# Revit family: Drain_Floor_Top_Diameter_9_Inch-Zurn-Z551-Medium-Duty
name_source: partatom
category: Plumbing Fixtures
units: mm (PartAtom-declared; Revit-internal decimal feet)

## family parameters
Always vertical = Yes
Cut with Voids When Loaded = No
Maintain Annotation Orientation = No
OmniClass Number = 23.45.55.21
OmniClass Title = Drains (Wastes)
Part Type = Normal
Room Calculation Point = No
Round Connector Dimension = Use Radius
Shared = No
Work Plane-Based = No

## types (33) — shared parameters
Assembly Code = D2030300
CW Connection = No
Default Elevation = 25 "
Description = 9 [229] DIAMETER TOP MEDIUM-DUTY DRAIN
Grate Open Area Sq.in = 18 "
HW Connection = No
Main Material = Iron - Zurn -Cast - Painted - Blue
Manufacturer = Zurn Water, LLC
Manufacurer Brand = Zurn
Modified Date = 11/21/2025
P Trap Primer Connetor = 0.25 "
Product Documentation Link = https://files.zurn.com
Product Page URL = https://www.zurn.com
Product data url = https://www.bimobject.com
URL = www.zurn.com
Vent Connection = No
WFU = 1
Waste Connection = Yes
Width = 12 "
zero-valued in all types: CWFU, HWFU

## per-type parameters (varying)
| type | Approx. Weight (Lbs) | Body Height (E) | Frame Dimension | Frame and Grate | Model | Outlet Connector Radius | Pipe Size A (Actual) | Pipe Size A (Inner Diameter) | Pipe Size A (Nominal Diameter) | Top Diameter | Top Diameter Inner | Type Comments | Z-Grate | ZN-Grate |
| Z551-2NH | 28 " | 4.75 " | 2 " | Iron - Zurn -Cast - Painted - Blue | Z551 | 1 " | 2.375 " | 2.067 " | 2 " | 9 " | 8.625 " | Z551-2 Inch-No Hub Outlet | Yes | No |
| Z551-2NL | 28 " | 3.5 " | 2 " | Iron - Zurn -Cast - Painted - Blue | Z551 | 1 " | 2.375 " | 2.067 " | 2 " | 9 " | 8.625 " | Z551-2 Inch -Neo Loc Outlet | Yes | No |
| Z551-3NH | 28 " | 4.75 " | 2 " | Iron - Zurn -Cast - Painted - Blue | Z551 | 1.5 " | 3.5 " | 3.068 " | 3 " | 9 " | 8.625 " | Z551-3 Inch -No-Hub Outlet | Yes | No |
| Z551-3NL | 28 " | 3.5 " | 2 " | Iron - Zurn -Cast - Painted - Blue | Z551 | 1.5 " | 3.5 " | 3.068 " | 3 " | 9 " | 8.625 " | Z551-3 Inch -Neo-Loc Outlet | Yes | No |
| Z551-3IC | 28 " | 3.75 " | 2 " | Iron - Zurn -Cast - Painted - Blue | Z551 | 1.5 " | 3.5 " | 3.068 " | 3 " | 9 " | 8.625 " | Z551-3 Inch -Inside Caulk Outlet | Yes | No |
| Z551-3IP | 28 " | 2.75 " | 2 " | Iron - Zurn -Cast - Painted - Blue | Z551 | 1.5 " | 3.5 " | 3.068 " | 3 " | 9 " | 8.625 " | Z551-3 Inch -Threaded Outlet | Yes | No |
| Z551-4IC | 28 " | 3.75 " | 2 " | Iron - Zurn -Cast - Painted - Blue | Z551 | 2 " | 4.5 " | 4.026 " | 4 " | 9 " | 8.625 " | Z551-4 Inch -Inside Caulk Outlet | Yes | No |
| Z551-4NH | 28 " | 4.75 " | 2 " | Iron - Zurn -Cast - Painted - Blue | Z551 | 2 " | 4.5 " | 4.026 " | 4 " | 9 " | 8.625 " | Z551-4 Inch -No-Hub Outlet | Yes | No |
| Z551-4IP | 28 " | 2.75 " | 2 " | Iron - Zurn -Cast - Painted - Blue | Z551 | 2 " | 4.5 " | 4.026 " | 4 " | 9 " | 8.625 " | Z551-4 Inch -Threaded Outlet | Yes | No |
| Z551-4NL | 28 " | 3.5 " | 2 " | Iron - Zurn -Cast - Painted - Blue | Z551 | 2 " | 4.5 " | 4.026 " | 4 " | 9 " | 8.625 " | Z551-4 Inch -Neo-Loc Outlet | Yes | No |
| Z551-6NH | 30 " | 5.25 " | 2 " | Iron - Zurn -Cast - Painted - Blue | Z551 | 3 " | 6.625 " | 6.065 " | 6 " | 9 " | 8.625 " | Z551-6 Inch -No Hub Outlet | Yes | No |
| ZB551-2NH | 28 " | 4.75 " | 2.188 " | Bronze - Zurn - Polished | ZB551 | 1 " | 2.375 " | 2.067 " | 2 " | 9.75 " | 9.375 " | ZB551-2 Inch-No Hub Outlet | No | Yes |
| ZB551-2NL | 28 " | 3.5 " | 2.188 " | Bronze - Zurn - Polished | ZB551 | 1 " | 2.375 " | 2.067 " | 2 " | 9.75 " | 9.375 " | ZB551-2 Inch -Neo Loc Outlet | No | Yes |
| ZB551-3NH | 28 " | 4.75 " | 2.188 " | Bronze - Zurn - Polished | ZB551 | 1.5 " | 3.5 " | 3.068 " | 3 " | 9.75 " | 9.375 " | ZB551-3 Inch -No-Hub Outlet | No | Yes |
| ZB551-3NL | 28 " | 3.5 " | 2.188 " | Bronze - Zurn - Polished | ZB551 | 1.5 " | 3.5 " | 3.068 " | 3 " | 9.75 " | 9.375 " | ZB551-3 Inch -Neo-Loc Outlet | No | Yes |
| ZB551-3IC | 28 " | 3.75 " | 2.188 " | Bronze - Zurn - Polished | ZB551 | 1.5 " | 3.5 " | 3.068 " | 3 " | 9.75 " | 9.375 " | ZB551-3 Inch -Inside Caulk Outlet | No | Yes |
| ZB551-3IP | 28 " | 2.75 " | 2.188 " | Bronze - Zurn - Polished | ZB551 | 1.5 " | 3.5 " | 3.068 " | 3 " | 9.75 " | 9.375 " | ZB551-3 Inch -Threaded Outlet | No | Yes |
| ZB551-4IC | 28 " | 3.75 " | 2.188 " | Bronze - Zurn - Polished | ZB551 | 2 " | 4.5 " | 4.026 " | 4 " | 9.75 " | 9.375 " | ZB551-4 Inch -Inside Caulk Outlet | No | Yes |
| ZB551-4NH | 28 " | 4.75 " | 2.188 " | Bronze - Zurn - Polished | ZB551 | 2 " | 4.5 " | 4.026 " | 4 " | 9.75 " | 9.375 " | ZB551-4 Inch -No-Hub Outlet | No | Yes |
| ZB551-4IP | 28 " | 2.75 " | 2.188 " | Bronze - Zurn - Polished | ZB551 | 2 " | 4.5 " | 4.026 " | 4 " | 9.75 " | 9.375 " | ZB551-4 Inch -Threaded Outlet | No | Yes |
| ZB551-4NL | 28 " | 3.5 " | 2.188 " | Bronze - Zurn - Polished | ZB551 | 2 " | 4.5 " | 4.026 " | 4 " | 9.75 " | 9.375 " | ZB551-4 Inch -Neo-Loc Outlet | No | Yes |
| ZB551-6NH | 30 " | 5.25 " | 2.188 " | Bronze - Zurn - Polished | ZB551 | 3 " | 6.625 " | 6.065 " | 6 " | 9.75 " | 9.375 " | ZB551-6 Inch -No Hub Outlet | No | Yes |
| ZN551-2NH | 28 " | 4.75 " | 2.188 " | Bronze - Zurn - Polished Nickel | ZN551 | 1 " | 2.375 " | 2.067 " | 2 " | 9.75 " | 9.375 " | ZN551-2 Inch-No Hub Outlet | No | Yes |
| ZN551-2NL | 28 " | 3.5 " | 2.188 " | Bronze - Zurn - Polished Nickel | ZN551 | 1 " | 2.375 " | 2.067 " | 2 " | 9.75 " | 9.375 " | ZN551-2 Inch -Neo Loc Outlet | No | Yes |
| ZN551-3NH | 28 " | 4.75 " | 2.188 " | Bronze - Zurn - Polished Nickel | ZN551 | 1.5 " | 3.5 " | 3.068 " | 3 " | 9.75 " | 9.375 " | ZN551-3 Inch -No-Hub Outlet | No | Yes |
| ZN551-3NL | 28 " | 3.5 " | 2.188 " | Bronze - Zurn - Polished Nickel | ZN551 | 1.5 " | 3.5 " | 3.068 " | 3 " | 9.75 " | 9.375 " | ZN551-3 Inch -Neo-Loc Outlet | No | Yes |
| ZN551-3IC | 28 " | 3.75 " | 2.188 " | Bronze - Zurn - Polished Nickel | ZN551 | 1.5 " | 3.5 " | 3.068 " | 3 " | 9.75 " | 9.375 " | ZN551-3 Inch -Inside Caulk Outlet | No | Yes |
| ZN551-3IP | 28 " | 2.75 " | 2.188 " | Bronze - Zurn - Polished Nickel | ZN551 | 1.5 " | 3.5 " | 3.068 " | 3 " | 9.75 " | 9.375 " | ZN551-3 Inch -Threaded Outlet | No | Yes |
| ZN551-4IC | 28 " | 3.75 " | 2.188 " | Bronze - Zurn - Polished Nickel | ZN551 | 2 " | 4.5 " | 4.026 " | 4 " | 9.75 " | 9.375 " | ZN551-4 Inch -Inside Caulk Outlet | No | Yes |
| ZN551-4NH | 28 " | 4.75 " | 2.188 " | Bronze - Zurn - Polished Nickel | ZN551 | 2 " | 4.5 " | 4.026 " | 4 " | 9.75 " | 9.375 " | ZN551-4 Inch -No-Hub Outlet | No | Yes |
| ZN551-4IP | 28 " | 2.75 " | 2.188 " | Bronze - Zurn - Polished Nickel | ZN551 | 2 " | 4.5 " | 4.026 " | 4 " | 9.75 " | 9.375 " | ZN551-4 Inch -Threaded Outlet | No | Yes |
| ZN551-4NL | 28 " | 3.5 " | 2.188 " | Bronze - Zurn - Polished Nickel | ZN551 | 2 " | 4.5 " | 4.026 " | 4 " | 9.75 " | 9.375 " | ZN551-4 Inch -Neo-Loc Outlet | No | Yes |
| ZN551-6NH | 30 " | 5.25 " | 2.188 " | Bronze - Zurn - Polished Nickel | ZN551 | 3 " | 6.625 " | 6.065 " | 6 " | 9.75 " | 9.375 " | ZN551-6 Inch -No Hub Outlet | No | Yes |

## geometry (parser evidence)
native form markers: Sweep x6
no freeform markers — native parametric forms only
